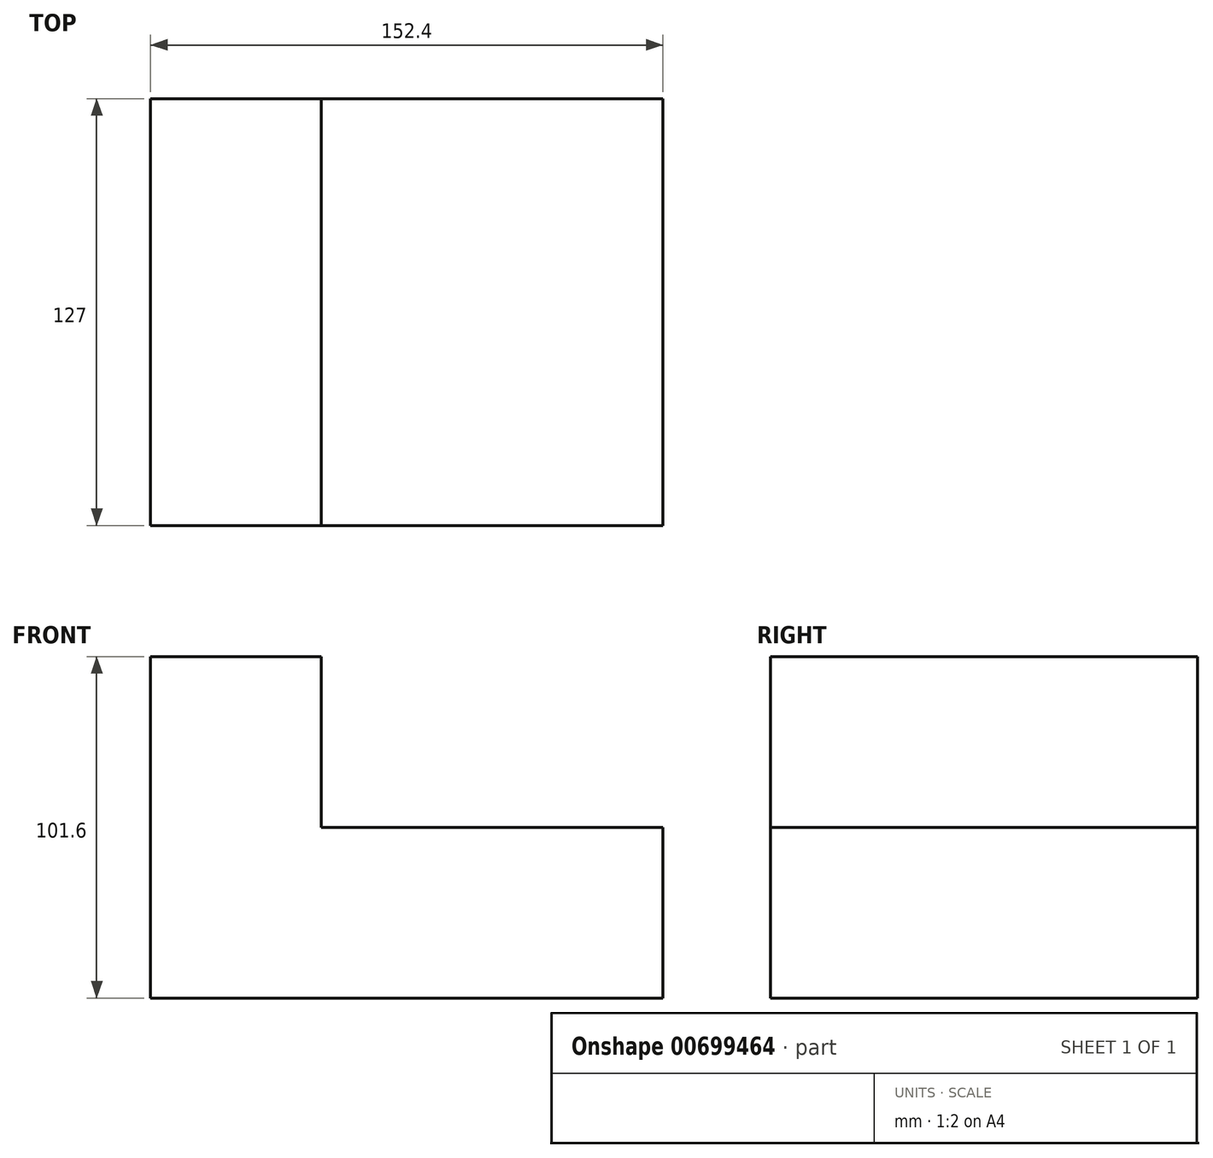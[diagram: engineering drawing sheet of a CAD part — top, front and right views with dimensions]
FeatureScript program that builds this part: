
annotation { "Feature Type Name" : "Feature", "Feature Type Description" : "" }
export const myFeature = defineFeature(function(context is Context, id is Id, definition is map)
    precondition{}
    {
        {
            var Q0;
            Q0=qCreatedBy(makeId("Front.planeOp"),FACE);
            var sketch = newSketch(context, id + "F0", { "sketchPlane" : qUnion([Q0])});
            skLineSegment(sketch, "E0", {"start": v(-142.06, -52.42) * mm, "end": v(10.34, -52.42) * mm});
            skLineSegment(sketch, "E1", {"start": v(10.34, -52.42) * mm, "end": v(10.34, -1.62) * mm});
            skLineSegment(sketch, "E2", {"start": v(10.34, -1.62) * mm, "end": v(-91.26, -1.62) * mm});
            skLineSegment(sketch, "E3", {"start": v(-91.26, -1.62) * mm, "end": v(-91.26, 49.18) * mm});
            skLineSegment(sketch, "E4", {"start": v(-91.26, 49.18) * mm, "end": v(-142.06, 49.18) * mm});
            skLineSegment(sketch, "E5", {"start": v(-142.06, 49.18) * mm, "end": v(-142.06, -52.42) * mm});
            skSolve(sketch);
        }
        {
            var Q0;
            Q0=makeQuery(id+"F0.imprint","IMPRINT",FACE,{"disambiguationData":[TD([[makeQuery(id+"F0.imprint","IMPRINT",EDGE,{"derivedFrom":sQuery(id+"F0.wireOp",EDGE,"E0")}),1.0]])]});
            extrude(context, id + "F1", {"entities" : qUnion([Q0]), "depth" : 127 * mm, "offsetDistance" : 25.4 * mm});
        }
    });
